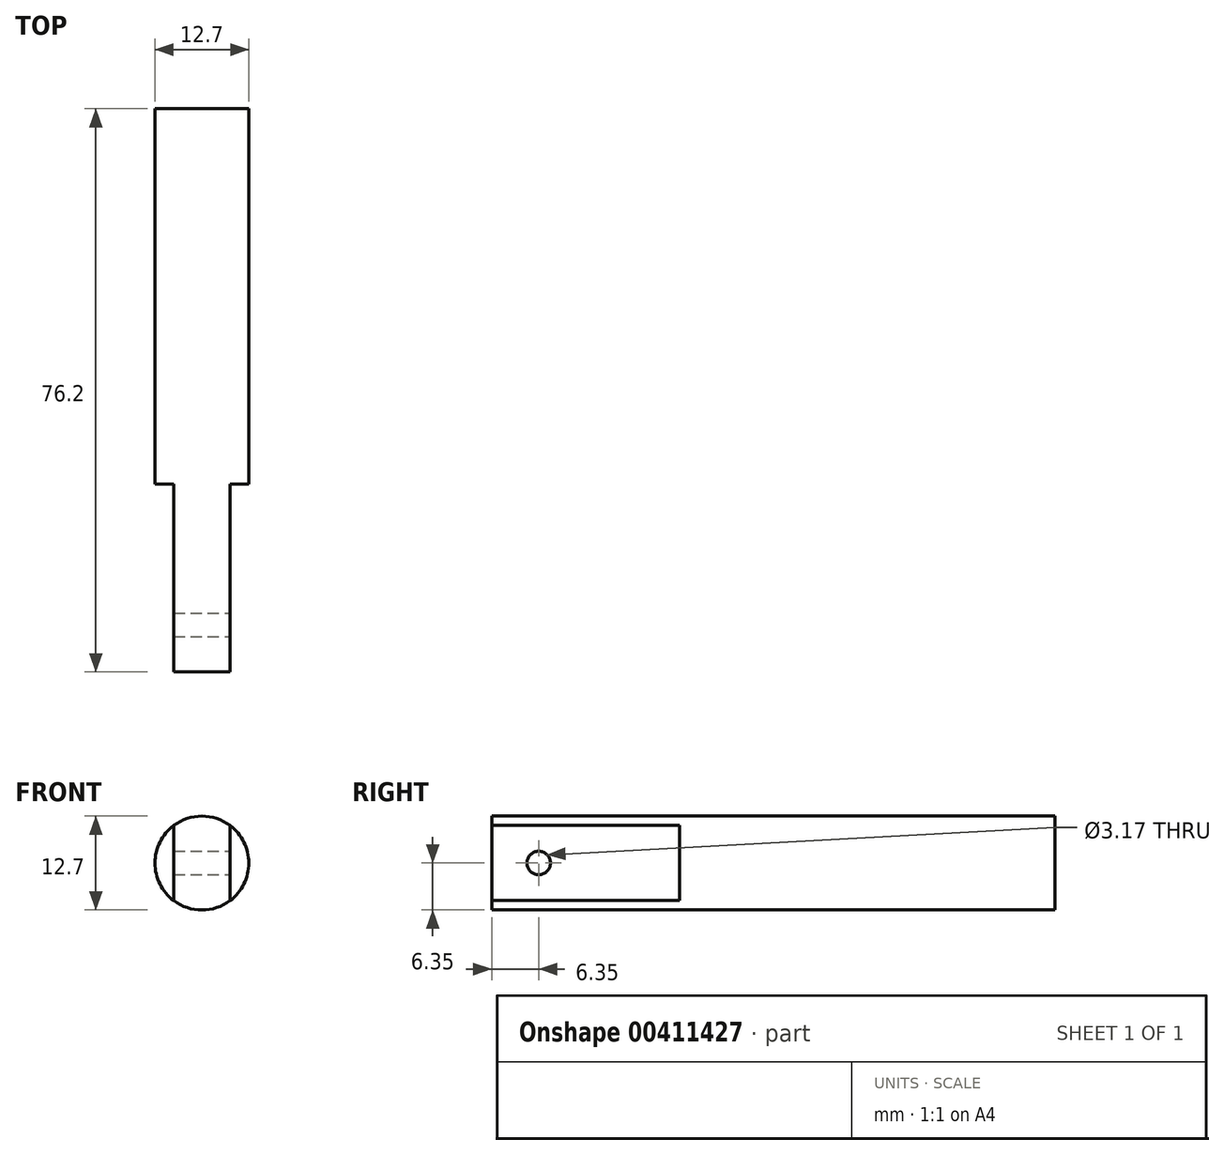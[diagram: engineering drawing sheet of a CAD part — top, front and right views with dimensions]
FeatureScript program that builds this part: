
annotation { "Feature Type Name" : "Feature", "Feature Type Description" : "" }
export const myFeature = defineFeature(function(context is Context, id is Id, definition is map)
    precondition{}
    {
        {
            var Q0;
            Q0=qCreatedBy(makeId("Front.planeOp"),FACE);
            var sketch = newSketch(context, id + "F0", { "sketchPlane" : qUnion([Q0])});
            skCircle(sketch, "E0", {"center": v(0, 0) * mm, "radius": 6.35 * mm});
            skSolve(sketch);
        }
        {
            var Q0;
            Q0 = qSketchRegion(id + "F0", true);
            extrude(context, id + "F1", {"entities" : qUnion([Q0]), "depth" : 76.2 * mm});
        }
        {
            var Q0;
            Q0=makeQuery(id+"F1.opExtrude","CAP_FACE",FACE,{"disambiguationData":[OSD([sQuery(id+"F0.wireOp",EDGE,"E0")])],"isStart":false});
            var sketch = newSketch(context, id + "F2", { "sketchPlane" : qUnion([Q0])});
            skLineSegment(sketch, "E1", {"start": v(3.8, 5.08) * mm, "end": v(3.81, -5.08) * mm});
            skLineSegment(sketch, "E2", {"start": v(-3.8, 5.08) * mm, "end": v(-3.81, -5.08) * mm});
            skArc(sketch, "E3", {"start": v(-3.81, 5.08) * mm, "mid": v(-6.35, 0) * mm, "end": v(-3.81, -5.08) * mm});
            skArc(sketch, "E4.trimOffspring", {"start": v(3.8, -5.08) * mm, "mid": v(6.35, 0) * mm, "end": v(3.8, 5.08) * mm});
            skSolve(sketch);
        }
        {
            var Q0;
            Q0 = qSketchRegion(id + "F2", true);
            extrude(context, id + "F3", {"entities" : qUnion([Q0]), "operationType" : NewBodyOperationType.REMOVE, "oppositeDirection" : true, "depth" : 25.4 * mm});
        }
        {
            var Q0;
            Q0=makeQuery(id+"F3.boolean.opBoolean","COPY",FACE,{"derivedFrom":makeQuery(id+"F3.opExtrude","SWEPT_FACE",FACE,{"disambiguationData":[OSD([sQuery(id+"F2.wireOp",EDGE,"E1")])]})});
            var sketch = newSketch(context, id + "F4", { "sketchPlane" : qUnion([Q0])});
            skCircle(sketch, "E5", {"center": v(-69.85, 0) * mm, "radius": 1.59 * mm});
            skSolve(sketch);
        }
        {
            var Q0;
            Q0 = qSketchRegion(id + "F4", true);
            extrude(context, id + "F5", {"entities" : qUnion([Q0]), "operationType" : NewBodyOperationType.REMOVE, "oppositeDirection" : true, "depth" : 25.4 * mm});
        }
    });
